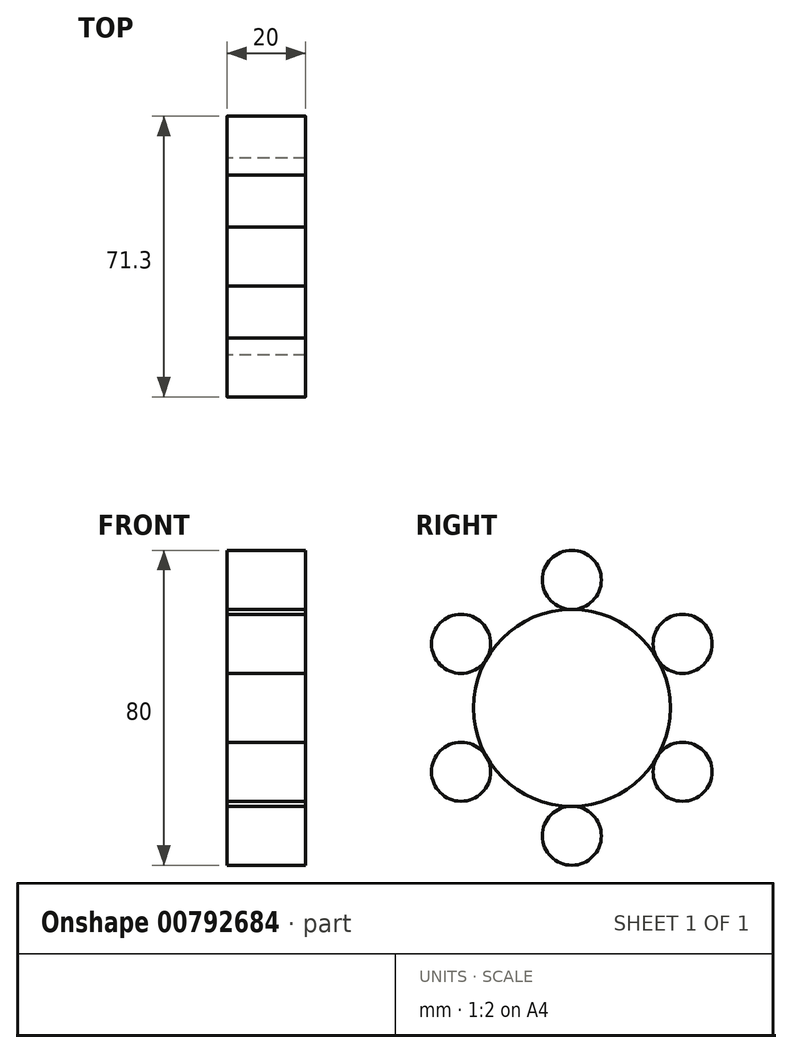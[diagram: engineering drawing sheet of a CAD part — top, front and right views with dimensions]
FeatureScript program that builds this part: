
annotation { "Feature Type Name" : "Feature", "Feature Type Description" : "" }
export const myFeature = defineFeature(function(context is Context, id is Id, definition is map)
    precondition{}
    {
        {
            var Q0;
            Q0=qCreatedBy(makeId("Right.planeOp"),FACE);
            var sketch = newSketch(context, id + "F0", { "sketchPlane" : qUnion([Q0])});
            skCircle(sketch, "E0", {"center": v(0, 0) * mm, "radius": 25 * mm});
            skCircle(sketch, "E1", {"center": v(0, -32.5) * mm, "radius": 7.5 * mm});
            skSolve(sketch);
        }
        {
            var Q0;
            Q0=makeQuery(id+"F0.imprint","IMPRINT",FACE,{"disambiguationData":[TD([[makeQuery(id+"F0.imprint","IMPRINT",EDGE,{"derivedFrom":sQuery(id+"F0.wireOp",EDGE,"E0")}),1.0]])]});
            var Q1;
            Q1=makeQuery(id+"F0.imprint","IMPRINT",FACE,{"disambiguationData":[TD([[makeQuery(id+"F0.imprint","IMPRINT",EDGE,{"derivedFrom":sQuery(id+"F0.wireOp",EDGE,"E1")}),1.0]])]});
            extrude(context, id + "F1", {"entities" : qUnion([Q0, Q1]), "depth" : 20 * mm, "offsetDistance" : 25 * mm});
        }
        {
            var Q0;
            Q0=makeQuery(id+"F1.opExtrude","SWEPT_BODY",BODY,{"disambiguationData":[OSD([sQuery(id+"F0.wireOp",EDGE,"E1")])]});
            var Q1;
            Q1=makeQuery(id+"F1.opExtrude","CAP_EDGE",EDGE,{"disambiguationData":[OSD([sQuery(id+"F0.wireOp",EDGE,"E0")])],"isStart":false});
            circularPattern(context, id + "F2", {"entities" : qUnion([Q0]), "axis" : qUnion([Q1]), "angle" : 360 * degree, "instanceCount" : 6, "equalSpace" : true});
        }
    });
